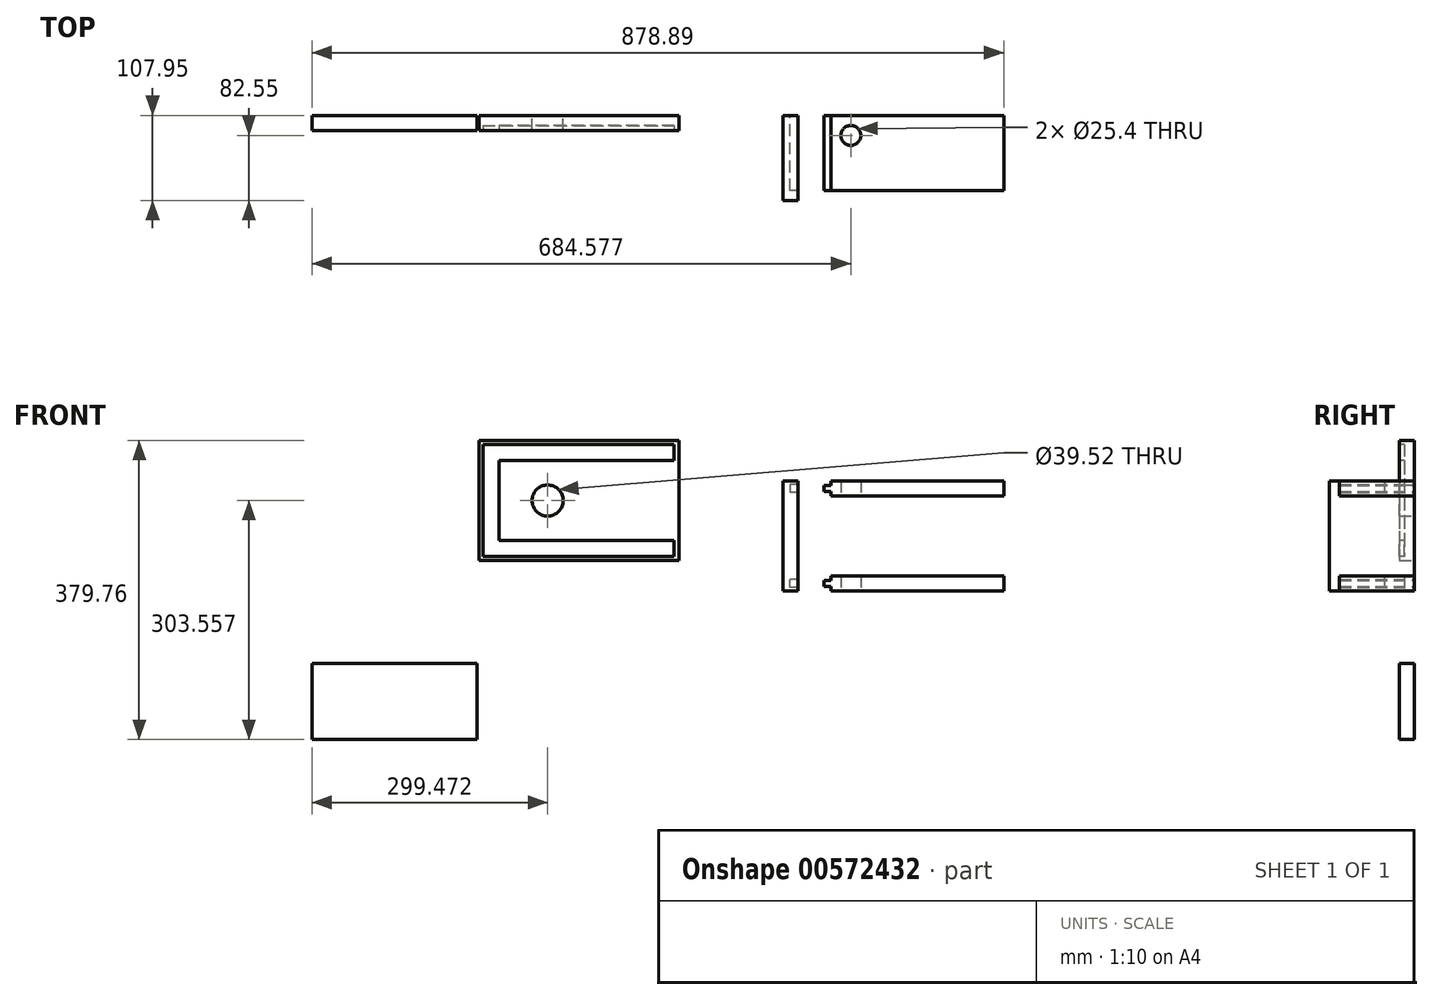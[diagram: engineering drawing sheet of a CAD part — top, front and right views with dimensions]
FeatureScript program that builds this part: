
annotation { "Feature Type Name" : "Feature", "Feature Type Description" : "" }
export const myFeature = defineFeature(function(context is Context, id is Id, definition is map)
    precondition{}
    {
        {
            var Q0;
            Q0=qCreatedBy(makeId("Front.planeOp"),FACE);
            var sketch = newSketch(context, id + "F0", { "sketchPlane" : qUnion([Q0])});
            skLineSegment(sketch, "E0.bottom", {"start": v(-79.82, 121.34) * mm, "end": v(174.18, 121.34) * mm});
            skLineSegment(sketch, "E0.top", {"start": v(-79.82, -31.06) * mm, "end": v(174.18, -31.06) * mm});
            skLineSegment(sketch, "E0.left", {"start": v(-79.82, 121.34) * mm, "end": v(-79.82, -31.06) * mm});
            skLineSegment(sketch, "E0.right", {"start": v(174.18, 121.34) * mm, "end": v(174.18, -31.06) * mm});
            skPoint(sketch, "E1", {"position": v(-54.42, 121.34) * mm});
            skPoint(sketch, "E2", {"position": v(-54.42, -31.06) * mm});
            skPoint(sketch, "E3", {"position": v(-54.42, -5.66) * mm});
            skLineSegment(sketch, "E4", {"start": v(47.18, 121.34) * mm, "end": v(47.18, -31.06) * mm, "construction": true});
            skLineSegment(sketch, "E5", {"start": v(-79.82, 45.14) * mm, "end": v(174.18, 45.14) * mm, "construction": true});
            skPoint(sketch, "E6.MirrorP", {"position": v(-54.42, 95.94) * mm});
            skLineSegment(sketch, "E7", {"start": v(-54.42, 95.94) * mm, "end": v(-54.42, -5.66) * mm});
            skLineSegment(sketch, "E8", {"start": v(174.18, -5.66) * mm, "end": v(-54.42, -5.66) * mm});
            skLineSegment(sketch, "E9", {"start": v(-54.42, 95.94) * mm, "end": v(174.18, 95.94) * mm});
            skLineSegment(sketch, "E10", {"start": v(-74.74, 116.26) * mm, "end": v(174.18, 116.26) * mm});
            skLineSegment(sketch, "E11.MirrorCS", {"start": v(-74.74, -25.98) * mm, "end": v(174.18, -25.98) * mm});
            skLineSegment(sketch, "E12", {"start": v(-74.74, 116.26) * mm, "end": v(-74.74, -25.98) * mm});
            skLineSegment(sketch, "E13", {"start": v(-54.42, 95.94) * mm, "end": v(-54.42, 116.26) * mm, "construction": true});
            skLineSegment(sketch, "E14", {"start": v(-54.42, -5.66) * mm, "end": v(-54.42, -25.98) * mm});
            skPoint(sketch, "E14.endSnap0", {"position": v(49.72, -25.98) * mm});
            skPoint(sketch, "E15", {"position": v(167.83, 116.26) * mm});
            skLineSegment(sketch, "E16", {"start": v(167.83, 116.26) * mm, "end": v(167.83, 95.94) * mm});
            skLineSegment(sketch, "E17.MirrorCS", {"start": v(167.83, -25.98) * mm, "end": v(167.83, -5.66) * mm});
            skCircle(sketch, "E18", {"center": v(7.31, 45.14) * mm, "radius": 19.76 * mm});
            skLineSegment(sketch, "E19", {"start": v(306.27, 70.02) * mm, "end": v(325.32, 70.02) * mm});
            skLineSegment(sketch, "E20", {"start": v(306.27, 70.02) * mm, "end": v(306.27, -69.68) * mm});
            skLineSegment(sketch, "E21", {"start": v(315.8, 70.02) * mm, "end": v(315.8, -69.68) * mm, "construction": true});
            skLineSegment(sketch, "E22", {"start": v(306.27, 0.17) * mm, "end": v(325.32, 0.17) * mm, "construction": true});
            skPoint(sketch, "E22.endSnap0", {"position": v(306.27, 0.17) * mm});
            skLineSegment(sketch, "E23.MirrorCS", {"start": v(306.27, -69.68) * mm, "end": v(325.32, -69.68) * mm});
            skLineSegment(sketch, "E24", {"start": v(325.32, 70.02) * mm, "end": v(325.32, -69.68) * mm});
            skPoint(sketch, "E25", {"position": v(325.32, 50.97) * mm});
            skPoint(sketch, "E26", {"position": v(325.32, 65.58) * mm});
            skPoint(sketch, "E27", {"position": v(325.32, 55.42) * mm});
            skPoint(sketch, "E28.MirrorP", {"position": v(325.32, -50.63) * mm});
            skPoint(sketch, "E29.MirrorP", {"position": v(325.32, -55.07) * mm});
            skLineSegment(sketch, "E30", {"start": v(367.02, 70.02) * mm, "end": v(367.02, 50.97) * mm});
            skLineSegment(sketch, "E31", {"start": v(367.02, 70.02) * mm, "end": v(586.73, 70.02) * mm});
            skLineSegment(sketch, "E32", {"start": v(367.02, 60.5) * mm, "end": v(586.73, 60.5) * mm, "construction": true});
            skLineSegment(sketch, "E33", {"start": v(476.87, 70.02) * mm, "end": v(476.87, 50.97) * mm, "construction": true});
            skLineSegment(sketch, "E34.MirrorCS", {"start": v(586.73, 70.02) * mm, "end": v(586.73, 50.97) * mm});
            skLineSegment(sketch, "E35.MirrorCS", {"start": v(367.02, 50.97) * mm, "end": v(586.73, 50.97) * mm});
            skLineSegment(sketch, "E36", {"start": v(325.32, 50.97) * mm, "end": v(367.02, 50.97) * mm, "construction": true});
            skLineSegment(sketch, "E37", {"start": v(325.32, 70.02) * mm, "end": v(367.02, 70.02) * mm, "construction": true});
            skLineSegment(sketch, "E38", {"start": v(346.17, 70.02) * mm, "end": v(346.17, 50.97) * mm, "construction": true});
            skLineSegment(sketch, "E39.MirrorCS", {"start": v(325.32, 65.58) * mm, "end": v(315.18, 65.58) * mm});
            skLineSegment(sketch, "E40.MirrorCS", {"start": v(325.32, 55.42) * mm, "end": v(315.18, 55.42) * mm});
            skLineSegment(sketch, "E41.MirrorCS", {"start": v(315.18, 65.58) * mm, "end": v(315.18, 55.42) * mm});
            skPoint(sketch, "E42", {"position": v(367.02, 64.3) * mm});
            skPoint(sketch, "E43.MirrorP", {"position": v(367.02, 56.69) * mm});
            skLineSegment(sketch, "E44.MirrorCS", {"start": v(367.02, 64.3) * mm, "end": v(358.13, 64.3) * mm});
            skLineSegment(sketch, "E45.MirrorCS", {"start": v(367.02, 56.69) * mm, "end": v(358.13, 56.69) * mm});
            skLineSegment(sketch, "E46", {"start": v(358.13, 64.3) * mm, "end": v(358.13, 56.69) * mm});
            skLineSegment(sketch, "E47.MirrorCS", {"start": v(367.02, -50.63) * mm, "end": v(586.73, -50.63) * mm});
            skLineSegment(sketch, "E48.MirrorCS", {"start": v(367.02, -69.68) * mm, "end": v(586.73, -69.68) * mm});
            skLineSegment(sketch, "E49.MirrorCS", {"start": v(586.73, -69.68) * mm, "end": v(586.73, -50.63) * mm});
            skLineSegment(sketch, "E50.MirrorCS", {"start": v(367.02, -69.68) * mm, "end": v(367.02, -50.63) * mm});
            skLineSegment(sketch, "E51.MirrorCS", {"start": v(367.02, -63.96) * mm, "end": v(358.13, -63.96) * mm});
            skLineSegment(sketch, "E52.MirrorCS", {"start": v(358.13, -63.96) * mm, "end": v(358.13, -56.34) * mm});
            skLineSegment(sketch, "E53.MirrorCS", {"start": v(367.02, -56.34) * mm, "end": v(358.13, -56.34) * mm});
            skLineSegment(sketch, "E54.MirrorCS", {"start": v(325.32, -55.07) * mm, "end": v(315.18, -55.07) * mm});
            skLineSegment(sketch, "E55.MirrorCS", {"start": v(325.32, -65.23) * mm, "end": v(315.18, -65.23) * mm});
            skLineSegment(sketch, "E56.MirrorCS", {"start": v(315.18, -65.23) * mm, "end": v(315.18, -55.07) * mm});
            skLineSegment(sketch, "E57.bottom", {"start": v(-292.16, -161.9) * mm, "end": v(-82.6, -161.9) * mm});
            skLineSegment(sketch, "E57.top", {"start": v(-292.16, -258.42) * mm, "end": v(-82.6, -258.42) * mm});
            skLineSegment(sketch, "E57.left", {"start": v(-292.16, -161.9) * mm, "end": v(-292.16, -258.42) * mm});
            skLineSegment(sketch, "E57.right", {"start": v(-82.6, -161.9) * mm, "end": v(-82.6, -258.42) * mm});
            skSolve(sketch);
        }
        {
            var Q0;
            {var subQ4=sQuery(id+"F0.wireOp",EDGE,"E7");Q0=makeQuery(id+"F0.imprint","IMPRINT",FACE,{"disambiguationData":[TD([[makeQuery(id+"F0.imprint","IMPRINT",EDGE,{"derivedFrom":subQ4}),-1.0]])]});}
            var Q1;
            {var subQ4=sQuery(id+"F0.wireOp",EDGE,"E7");Q1=makeQuery(id+"F0.imprint","IMPRINT",FACE,{"disambiguationData":[TD([[makeQuery(id+"F0.imprint","IMPRINT",EDGE,{"derivedFrom":subQ4}),1.0]])]});}
            var Q2;
            {var subQ0=sQuery(id+"F0.wireOp",EDGE,"E14");Q2=makeQuery(id+"F0.imprint","IMPRINT",FACE,{"disambiguationData":[TD([[makeQuery(id+"F0.imprint","IMPRINT",EDGE,{"derivedFrom":subQ0}),1.0]])]});}
            var Q3;
            {var subQ7=sQuery(id+"F0.wireOp",EDGE,"E0.bottom");Q3=makeQuery(id+"F0.imprint","IMPRINT",FACE,{"disambiguationData":[TD([[makeQuery(id+"F0.imprint","IMPRINT",EDGE,{"derivedFrom":subQ7}),-1.0]])]});}
            var Q4;
            {var subQ5=sQuery(id+"F0.wireOp",EDGE,"E16");Q4=makeQuery(id+"F0.imprint","IMPRINT",FACE,{"disambiguationData":[TD([[makeQuery(id+"F0.imprint","IMPRINT",EDGE,{"derivedFrom":subQ5}),1.0]])]});}
            var Q5;
            {var subQ5=sQuery(id+"F0.wireOp",EDGE,"E17.MirrorCS");Q5=makeQuery(id+"F0.imprint","IMPRINT",FACE,{"disambiguationData":[TD([[makeQuery(id+"F0.imprint","IMPRINT",EDGE,{"derivedFrom":subQ5}),-1.0]])]});}
            extrude(context, id + "F1", {"entities" : qUnion([Q0, Q1, Q2, Q3, Q4, Q5]), "depth" : 19.05 * mm, "offsetDistance" : 25.4 * mm});
        }
        {
            var Q0;
            Q0=makeQuery(id+"F1.opExtrude","CAP_FACE",FACE,{"disambiguationData":[OSD([sQuery(id+"F0.wireOp",EDGE,"E0.bottom"),sQuery(id+"F0.wireOp",EDGE,"E0.top"),sQuery(id+"F0.wireOp",EDGE,"E0.left"),sQuery(id+"F0.wireOp",EDGE,"E0.right")])],"isStart":false});
            var sketch = newSketch(context, id + "F2", { "sketchPlane" : qUnion([Q0])});
            skLineSegment(sketch, "E58.0", {"start": v(-74.74, 116.26) * mm, "end": v(-74.74, -25.98) * mm});
            skLineSegment(sketch, "E59.0", {"start": v(-74.74, 116.26) * mm, "end": v(174.18, 116.26) * mm});
            skLineSegment(sketch, "E60.0", {"start": v(-54.42, 95.94) * mm, "end": v(174.18, 95.94) * mm});
            skLineSegment(sketch, "E60.1", {"start": v(167.83, 116.26) * mm, "end": v(167.83, 95.94) * mm});
            skLineSegment(sketch, "E60.2", {"start": v(-54.42, 95.94) * mm, "end": v(-54.42, 116.26) * mm});
            skLineSegment(sketch, "E60.3", {"start": v(-54.42, 95.94) * mm, "end": v(-54.42, -5.66) * mm});
            skLineSegment(sketch, "E60.4", {"start": v(-54.42, -5.66) * mm, "end": v(-54.42, -25.98) * mm});
            skLineSegment(sketch, "E61.0", {"start": v(-74.74, -25.98) * mm, "end": v(174.18, -25.98) * mm});
            skLineSegment(sketch, "E62.0", {"start": v(174.18, -5.66) * mm, "end": v(-54.42, -5.66) * mm});
            skLineSegment(sketch, "E63.0", {"start": v(167.83, -25.98) * mm, "end": v(167.83, -5.66) * mm});
            skSolve(sketch);
        }
        {
            var Q0;
            Q0 = qSketchRegion(id + "F2", true);
            extrude(context, id + "F3", {"entities" : qUnion([Q0]), "operationType" : NewBodyOperationType.REMOVE, "oppositeDirection" : true, "depth" : 6.35 * mm, "offsetDistance" : 25.4 * mm});
        }
        {
            var Q0;
            {var subQ1=sQuery(id+"F0.wireOp",EDGE,"E19");Q0=makeQuery(id+"F0.imprint","IMPRINT",FACE,{"disambiguationData":[TD([[makeQuery(id+"F0.imprint","IMPRINT",EDGE,{"derivedFrom":subQ1}),-1.0]])]});}
            var Q1;
            {var subQ0=sQuery(id+"F0.wireOp",EDGE,"8OoexnOx-7CJ1-QHFI-KxOR-Xyc3CDSFZyaE");Q1=makeQuery(id+"F0.imprint","IMPRINT",FACE,{"disambiguationData":[TD([[makeQuery(id+"F0.imprint","IMPRINT",EDGE,{"derivedFrom":subQ0}),-1.0]])]});}
            var Q2;
            {var subQ0=sQuery(id+"F0.wireOp",EDGE,"0970f7c7-1c14-47e9-8dbc-feefddf68df10.MirrorCS");Q2=makeQuery(id+"F0.imprint","IMPRINT",FACE,{"disambiguationData":[TD([[makeQuery(id+"F0.imprint","IMPRINT",EDGE,{"derivedFrom":subQ0}),1.0]])]});}
            var Q3;
            {var subQ0=sQuery(id+"F0.wireOp",EDGE,"E31");Q3=makeQuery(id+"F0.imprint","IMPRINT",FACE,{"disambiguationData":[TD([[makeQuery(id+"F0.imprint","IMPRINT",EDGE,{"derivedFrom":subQ0}),-1.0]])]});}
            var Q4;
            {var subQ3=sQuery(id+"F0.wireOp",EDGE,"E47.MirrorCS");Q4=makeQuery(id+"F0.imprint","IMPRINT",FACE,{"disambiguationData":[TD([[makeQuery(id+"F0.imprint","IMPRINT",EDGE,{"derivedFrom":subQ3}),-1.0]])]});}
            var Q5;
            {var subQ0=sQuery(id+"F0.wireOp",EDGE,"E44.MirrorCS");Q5=makeQuery(id+"F0.imprint","IMPRINT",FACE,{"disambiguationData":[TD([[makeQuery(id+"F0.imprint","IMPRINT",EDGE,{"derivedFrom":subQ0}),1.0]])]});}
            var Q6;
            {var subQ0=sQuery(id+"F0.wireOp",EDGE,"E51.MirrorCS");Q6=makeQuery(id+"F0.imprint","IMPRINT",FACE,{"disambiguationData":[TD([[makeQuery(id+"F0.imprint","IMPRINT",EDGE,{"derivedFrom":subQ0}),-1.0]])]});}
            extrude(context, id + "F4", {"entities" : qUnion([Q0, Q1, Q2, Q3, Q4, Q5, Q6]), "depth" : 95.25 * mm, "offsetDistance" : 25.4 * mm});
        }
        {
            var Q0;
            Q0=makeQuery(id+"F4.opExtrude","SWEPT_FACE",FACE,{"disambiguationData":[OSD([sQuery(id+"F0.wireOp",EDGE,"E48.MirrorCS")])]});
            var sketch = newSketch(context, id + "F5", { "sketchPlane" : qUnion([Q0])});
            skPoint(sketch, "E64", {"position": v(586.73, 6.35) * mm});
            skPoint(sketch, "E65", {"position": v(586.73, 0) * mm});
            skLineSegment(sketch, "E66", {"start": v(586.73, 6.35) * mm, "end": v(367.02, 6.35) * mm});
            skPoint(sketch, "E67", {"position": v(392.42, 6.35) * mm});
            skLineSegment(sketch, "E68", {"start": v(392.42, 6.35) * mm, "end": v(392.42, 95.25) * mm, "construction": true});
            skPoint(sketch, "E69", {"position": v(367.02, 25.4) * mm});
            skLineSegment(sketch, "E70", {"start": v(367.02, 25.4) * mm, "end": v(586.73, 25.4) * mm, "construction": true});
            skCircle(sketch, "E71", {"center": v(392.42, 25.4) * mm, "radius": 12.7 * mm});
            skSolve(sketch);
        }
        {
            var Q0;
            Q0=makeQuery(id+"F5.imprint","IMPRINT",FACE,{"disambiguationData":[TD([[makeQuery(id+"F5.imprint","IMPRINT",EDGE,{"derivedFrom":sQuery(id+"F5.wireOp",EDGE,"E71")}),1.0]])]});
            extrude(context, id + "F6", {"entities" : qUnion([Q0]), "operationType" : NewBodyOperationType.REMOVE, "endBound" : BoundingType.THROUGH_ALL, "oppositeDirection" : true, "depth" : 206.5 * mm, "offsetDistance" : 25.4 * mm});
        }
        {
            var Q0;
            Q0=makeQuery(id+"F4.opExtrude","CAP_FACE",FACE,{"disambiguationData":[OSD([sQuery(id+"F0.wireOp",EDGE,"E19"),sQuery(id+"F0.wireOp",EDGE,"E20"),sQuery(id+"F0.wireOp",EDGE,"E23.MirrorCS"),sQuery(id+"F0.wireOp",EDGE,"E24"),sQuery(id+"F0.wireOp",EDGE,"E39.MirrorCS"),sQuery(id+"F0.wireOp",EDGE,"E40.MirrorCS"),sQuery(id+"F0.wireOp",EDGE,"E41.MirrorCS"),sQuery(id+"F0.wireOp",EDGE,"E54.MirrorCS"),sQuery(id+"F0.wireOp",EDGE,"E55.MirrorCS"),sQuery(id+"F0.wireOp",EDGE,"E56.MirrorCS")])],"isStart":false});
            var sketch = newSketch(context, id + "F7", { "sketchPlane" : qUnion([Q0])});
            skLineSegment(sketch, "E72.0", {"start": v(325.32, 70.02) * mm, "end": v(325.32, -69.68) * mm});
            skLineSegment(sketch, "E73.0", {"start": v(306.27, 70.02) * mm, "end": v(306.27, -69.68) * mm});
            skLineSegment(sketch, "E74.0", {"start": v(306.27, 70.02) * mm, "end": v(325.32, 70.02) * mm});
            skLineSegment(sketch, "E75.0", {"start": v(306.27, -69.68) * mm, "end": v(325.32, -69.68) * mm});
            skSolve(sketch);
        }
        {
            var Q0;
            Q0 = qSketchRegion(id + "F7", true);
            extrude(context, id + "F8", {"entities" : qUnion([Q0]), "operationType" : NewBodyOperationType.ADD, "depth" : 12.7 * mm, "offsetDistance" : 25.4 * mm});
        }
        {
            var Q0;
            Q0=makeQuery(id+"F0.imprint","IMPRINT",FACE,{"disambiguationData":[TD([[makeQuery(id+"F0.imprint","IMPRINT",EDGE,{"derivedFrom":sQuery(id+"F0.wireOp",EDGE,"E57.bottom")}),-1.0]])]});
            extrude(context, id + "F9", {"entities" : qUnion([Q0]), "depth" : 19.05 * mm, "offsetDistance" : 25.4 * mm});
        }
    });
